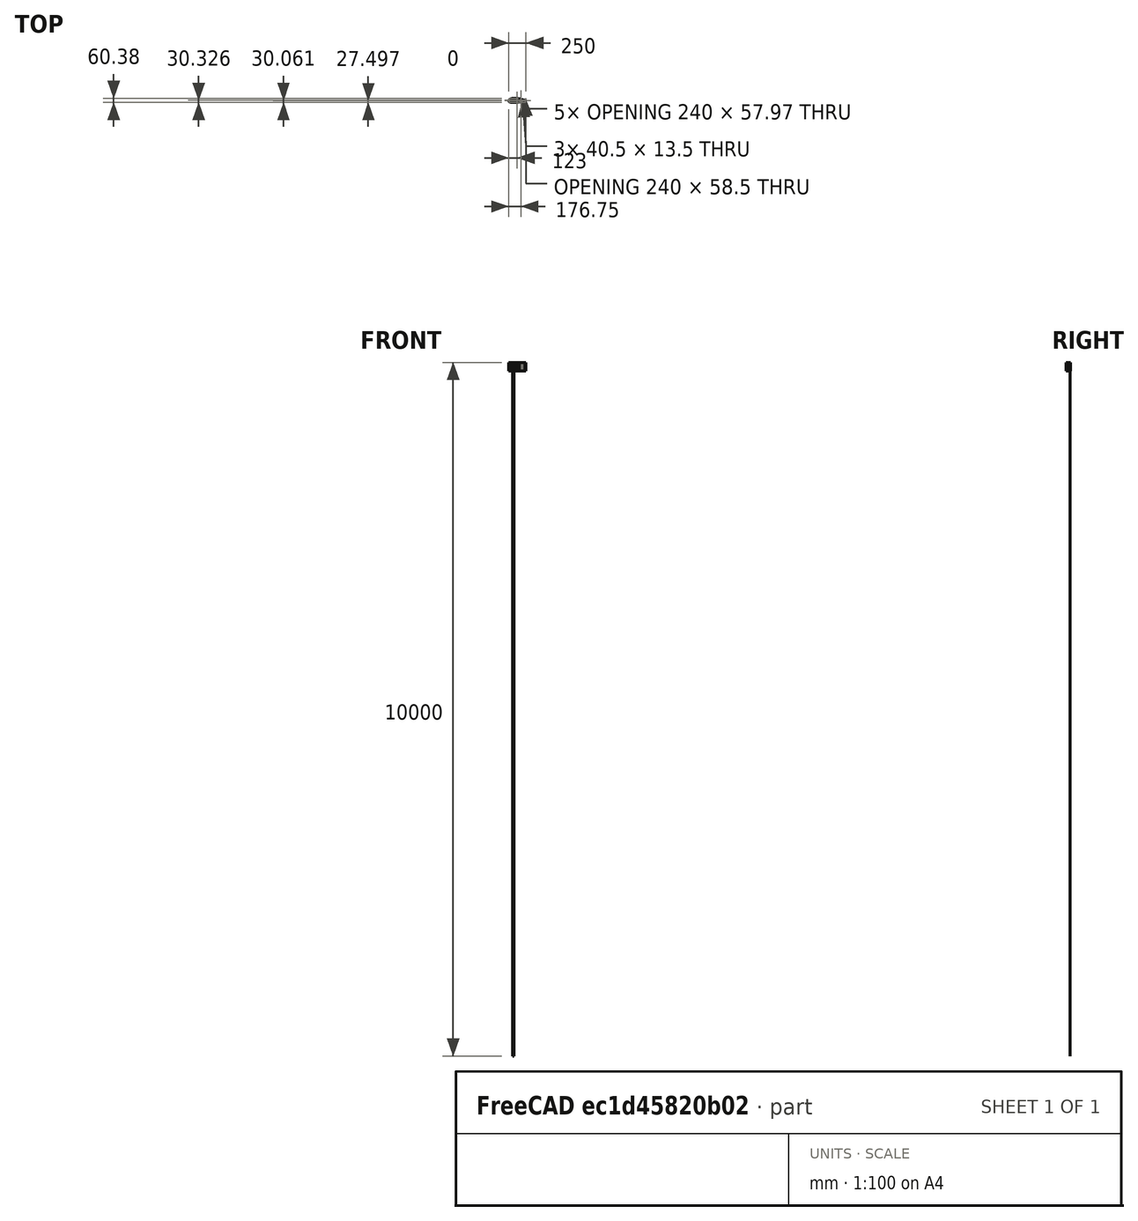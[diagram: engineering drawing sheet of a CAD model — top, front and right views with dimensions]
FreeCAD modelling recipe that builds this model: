
FCSTD DOCUMENT  (FreeCAD 0.16R6712 (Git))
Label: Corp
License: All rights reserved
LicenseURL: http://en.wikipedia.org/wiki/All_rights_reserved
objects: Sketcher::SketchObject×10, PartDesign::Pad×7, Mesh::Feature×7, PartDesign::Pocket×5, App::DocumentObjectGroup×2, Part::Part2DObjectPython×2, Part::Cut×1
note: 37 computed .brp shape members not serialized (recipe doc carries the construction recipe); baked Part::Feature solids carry a one-line shape summary decoded from their .brp

FEATURE [App::DocumentObjectGroup] naca4424
FEATURE [Part::Part2DObjectPython] DWire  # Draft 2D object (typed FeaturePython)
  ChamferSize = 0
  Closed = true
  End = (250,0,0)
  FilletRadius = 0
  Length = 531.973
  MakeFace = true
  Points = (34) [(237.99,5.6,0),(225.8,10.2475,0),(201.16,18.6175,0),(176.218,25.78,0),(151.012,31.685,0),(125.587,36.185,0),(100,39.015,0),(73.5025,39.345,0),+26 more]
  Start = (237.99,5.6,0)
  Subdivisions = 0
FEATURE [PartDesign::Pad] Pad
  Length = 120
  Length2 = 100
  Sketch = -> DWire
  Type = 0
FEATURE [App::DocumentObjectGroup] naca4424001  label="naca4424_interne"
FEATURE [Part::Part2DObjectPython] DWire001  # Draft 2D object (typed FeaturePython)
  ChamferSize = 0
  Closed = true
  End = (243,0.5,0)
  FilletRadius = 0
  Length = 510.694
  MakeFace = true
  Placement = pos=(3,0.5,0) rot=(0,0,1;0rad)
  Points = (34) [(228.47,5.376,0),(216.768,9.8376,0),(193.114,17.8728,0),(169.169,24.7488,0),(144.972,30.4176,0),(120.564,34.7376,0),(96,37.4544,0),+27 more]
  Start = (231.47,5.876,0)
  Subdivisions = 0
FEATURE [PartDesign::Pad] Pad001
  Length = 120
  Length2 = 100
  Placement = pos=(3,0.5,0) rot=(0,0,1;0rad)
  Sketch = -> DWire001
  Type = 0
FEATURE [Part::Cut] Cut  label="Enveloppe"
  Base = -> Pad
  Tool = -> Pad001
FEATURE [Sketcher::SketchObject] Sketch
  ExternalGeometry = -> [Cut]
  Placement = pos=(0,0,120) rot=(0,0,1;0rad)
  Support = -> Cut [Face5]
  sketch-geometry (36):
    g0: LineSegment StartX=25.94 StartY=27.8417 StartZ=0 EndX=25.94 EndY=-15.2288 EndZ=0
    g1: LineSegment StartX=37.1909 StartY=32.1712 StartZ=0 EndX=77 EndY=32.1712 EndZ=0
    g2: LineSegment StartX=25.94 StartY=-15.2288 StartZ=0 EndX=125.433 EndY=-15.2288 EndZ=0
    g3: LineSegment StartX=40.9721 StartY=33.1712 StartZ=0 EndX=77 EndY=33.1712 EndZ=0
    g4: LineSegment StartX=40.9721 StartY=33.1712 StartZ=0 EndX=37.1909 EndY=32.1712 EndZ=0
    g5: LineSegment StartX=135.239 StartY=33.1712 StartZ=0 EndX=140.889 EndY=32.1712 EndZ=0
    g6: LineSegment StartX=25.94 StartY=-16.2288 StartZ=0 EndX=116.78 EndY=-16.2288 EndZ=0
    g7: LineSegment StartX=125.433 StartY=-15.2288 StartZ=0 EndX=116.78 EndY=-16.2288 EndZ=0
    g8: LineSegment StartX=77 StartY=38.2284 StartZ=0 EndX=77 EndY=33.1712 EndZ=0
    g9: LineSegment StartX=77 StartY=30.2284 StartZ=0 EndX=116.5 EndY=30.2284 EndZ=0
    g10: LineSegment StartX=116.5 StartY=30.2284 StartZ=0 EndX=116.5 EndY=10.2284 EndZ=0
    g11: LineSegment StartX=116.5 StartY=10.2284 StartZ=0 EndX=117.5 EndY=10.2284 EndZ=0
    g12: LineSegment StartX=117.5 StartY=10.2284 StartZ=0 EndX=117.5 EndY=32.1712 EndZ=0
    g13: LineSegment StartX=78 StartY=38.2159 StartZ=0 EndX=78 EndY=31.2284 EndZ=0
    g14: LineSegment StartX=78 StartY=31.2284 StartZ=0 EndX=116.5 EndY=31.2284 EndZ=0
    g15: LineSegment StartX=116.5 StartY=31.2284 StartZ=0 EndX=116.5 EndY=36.0189 EndZ=0
    g16: LineSegment StartX=117.5 StartY=33.1712 StartZ=0 EndX=135.239 EndY=33.1712 EndZ=0
    g17: LineSegment StartX=117.5 StartY=32.1712 StartZ=0 EndX=140.889 EndY=32.1712 EndZ=0
    g18: LineSegment StartX=77 StartY=32.1712 StartZ=0 EndX=77 EndY=30.2284 EndZ=0
    g19: LineSegment StartX=117.5 StartY=33.1712 StartZ=0 EndX=117.5 EndY=35.9083 EndZ=0
    g20: LineSegment StartX=77 StartY=38.2284 StartZ=0 EndX=78 EndY=38.2159 EndZ=0
    g21: LineSegment StartX=116.5 StartY=36.0189 StartZ=0 EndX=117.5 EndY=35.9083 EndZ=0
    g22: Circle CenterX=5.5894 CenterY=1.00227 CenterZ=0 NormalX=0 NormalY=0 NormalZ=1 Radius=2.5
    g23: ArcOfCircle CenterX=5.5894 CenterY=1.00227 CenterZ=0 NormalX=0 NormalY=0 NormalZ=1 Radius=3.5 StartAngle=4.43289 EndAngle=8.51667
    g24: LineSegment StartX=3.43607 StartY=3.76147 StartZ=0 EndX=3 EndY=0.5 EndZ=0
    g25: LineSegment StartX=3 StartY=0.5 StartZ=0 EndX=4.62383 EndY=-2.3619 EndZ=0
    g26: Circle CenterX=234.867 CenterY=1.53378 CenterZ=0 NormalX=0 NormalY=0 NormalZ=1 Radius=2.5
    g27: ArcOfCircle CenterX=234.867 CenterY=1.53378 CenterZ=0 NormalX=0 NormalY=0 NormalZ=1 Radius=3.5 StartAngle=1.90968 EndAngle=4.12064
    g28: ArcOfCircle CenterX=234.867 CenterY=1.53378 CenterZ=0 NormalX=0 NormalY=0 NormalZ=1 Radius=3.5 StartAngle=5.67102 EndAngle=6.64248
    g29: LineSegment StartX=233.704 StartY=4.83472 StartZ=0 EndX=238.144 EndY=2.76443 EndZ=0
    g30: LineSegment StartX=232.915 StartY=-1.37109 StartZ=0 EndX=237.732 EndY=-0.477447 EndZ=0
    g31: LineSegment StartX=24.94 StartY=-16.296 StartZ=0 EndX=25.94 EndY=-16.5246 EndZ=0
    g32: LineSegment StartX=25.94 StartY=-16.5246 StartZ=0 EndX=25.94 EndY=-16.2288 EndZ=0
    g33: LineSegment StartX=24.94 StartY=27.4402 StartZ=0 EndX=25.94 EndY=27.8417 EndZ=0
    g34: LineSegment [constr] StartX=25.94 StartY=-15.2288 StartZ=0 EndX=25.94 EndY=-16.2288 EndZ=0
    g35: LineSegment StartX=24.94 StartY=27.4402 StartZ=0 EndX=24.94 EndY=-16.296 EndZ=0
  constraints (101):
    c: Vertical(g0)
    c: Horizontal(g1)
    c: Horizontal(g2)
    c: PointOnObject(g1,g-3)
    c: DistanceY(g1,g-4) = 6.1
    c: PointOnObject(g17,g-5)
    c: PointOnObject(g16,g-5)
    c: Horizontal(g3)
    c: PointOnObject(g3,g-3)
    c: Coincident(g4,g3)
    c: Coincident(g4,g1)
    c: Coincident(g5,g16)
    c: Coincident(g5,g17)
    c: DistanceY(g17,g16) = 1
    c: Horizontal(g6)
    c: PointOnObject(g2,g-8)
    c: PointOnObject(g6,g-8)
    c: Coincident(g7,g2)
    c: Coincident(g7,g6)
    c: Coincident(g0,g2)
    c: DistanceY(g6,g0) = 1
    c: Vertical(g8)
    c: Coincident(g9,g18)
    c: Horizontal(g9)
    c: Coincident(g10,g9)
    c: Vertical(g10)
    c: Coincident(g11,g10)
    c: Horizontal(g11)
    c: Vertical(g12)
    c: PointOnObject(g8,g-4)
    c: DistanceY(g18,g8) = 8
    c: DistanceX(g8,g-4) = 22
    c: DistanceX(g9,g9) = 39.5
    c: DistanceX(g11,g11) = 1
    c: Coincident(g11,g12)
    c: PointOnObject(g19,g-9)
    c: PointOnObject(g13,g-4)
    c: Vertical(g13)
    c: Coincident(g14,g13)
    c: Horizontal(g14)
    c: Coincident(g15,g14)
    c: PointOnObject(g15,g-9)
    c: Vertical(g15)
    c: Tangent(g3,g16)
    c: Tangent(g1,g17)
    c: Coincident(g8,g3)
    c: Coincident(g18,g1)
    c: Tangent(g8,g18)
    c: Coincident(g12,g17)
    c: Coincident(g19,g16)
    c: Tangent(g12,g19)
    c: DistanceX(g15,g19) = 1
    c: DistanceY(g9,g14) = 1
    c: DistanceX(g8,g13) = 1
    c: Coincident(g20,g8)
    c: Coincident(g20,g13)
    c: Coincident(g21,g15)
    c: Coincident(g21,g19)
    c: DistanceY(g10,g10) = 20
    c: Tangent(g22,g-10)
    c: Radius(g22) = 2.5
    c: Coincident(g23,g22)
    c: PointOnObject(g23,g-10)
    c: Coincident(g24,g-10)
    c: Tangent(g24,g22)
    c: Coincident(g25,g24)
    c: Coincident(g25,g23)
    c: Tangent(g26,g-11)
    c: Tangent(g26,g-12)
    c: Radius(g26) = 2.5
    c: Radius(g23) = 3.5
    c: Coincident(g27,g26)
    c: PointOnObject(g27,g-11)
    c: PointOnObject(g27,g-12)
    c: Radius(g27) = 3.5
    c: Coincident(g28,g26)
    c: PointOnObject(g28,g-11)
    c: PointOnObject(g28,g-12)
    c: Radius(g28) = 3.5
    c: Coincident(g29,g27)
    c: Coincident(g29,g28)
    c: Coincident(g30,g28)
    c: Coincident(g32,g6)
    c: Vertical(g32)
    c: Coincident(g33,g0)
    c: DistanceX(g33,g0) = 1
    c: Coincident(g30,g27)
    c: Coincident(g23,g24)
    c: PointOnObject(g23,g-13)
    c: DistanceX(g-7,g31) = 8
    c: PointOnObject(g0,g-6)
    c: PointOnObject(g33,g-6)
    c: PointOnObject(g31,g-16)
    c: Vertical(g34)
    c: Coincident(g34,g6)
    c: Coincident(g0,g34)
    c: DistanceX(g31,g31) = 1
    c: PointOnObject(g32,g-16)
    c: Coincident(g32,g31)
    c: Coincident(g35,g33)
    c: Coincident(g35,g31)
FEATURE [PartDesign::Pad] Pad002  label="Interne__Support_Composant"
  Length = 120
  Length2 = 100
  Reversed = true
  Sketch = -> Sketch
  Type = 0
FEATURE [Mesh::Feature] Support_Composant
  Placement = pos=(116,-15,119) rot=(0,1,0;3.14159rad)
FEATURE [Mesh::Feature] Gouverne_Profondeur
  Placement = pos=(252,1,-2.5) rot=(0,0,1;0rad)
FEATURE [Sketcher::SketchObject] Sketch001
  ExternalGeometry = -> [Pad002]
  Placement = pos=(0,0,0) rot=(1,0,0;3.14159rad)
  Support = -> Pad002 [Face4]
  sketch-geometry (20):
    g0: LineSegment StartX=156.5 StartY=11.529 StartZ=0 EndX=156.5 EndY=1.29344 EndZ=0
    g1: LineSegment StartX=156.5 StartY=11.529 StartZ=0 EndX=155.5 EndY=11.655 EndZ=0
    g2: LineSegment StartX=155.5 StartY=11.655 StartZ=0 EndX=155.5 EndY=-29.1539 EndZ=0
    g3: LineSegment StartX=155.5 StartY=-29.1539 StartZ=0 EndX=156.5 EndY=-28.9197 EndZ=0
    g4: LineSegment StartX=156.5 StartY=0.293445 StartZ=0 EndX=197 EndY=0.293445 EndZ=0
    g5: LineSegment StartX=156.5 StartY=1.29344 StartZ=0 EndX=197 EndY=1.29344 EndZ=0
    g6: LineSegment StartX=197 StartY=1.29344 StartZ=0 EndX=197 EndY=6.29344 EndZ=0
    g7: LineSegment StartX=197 StartY=6.29344 StartZ=0 EndX=198 EndY=6.16056 EndZ=0
    g8: LineSegment StartX=198 StartY=6.16056 StartZ=0 EndX=198 EndY=-17.732 EndZ=0
    g9: LineSegment StartX=197 StartY=0.293445 StartZ=0 EndX=197 EndY=-13.2066 EndZ=0
    g10: LineSegment StartX=197 StartY=-18.0717 StartZ=0 EndX=198 EndY=-17.732 EndZ=0
    g11: LineSegment StartX=156.5 StartY=0.293445 StartZ=0 EndX=156.5 EndY=-13.2066 EndZ=0
    g12: LineSegment [constr] StartX=197 StartY=1.29344 StartZ=0 EndX=197 EndY=0.293445 EndZ=0
    g13: LineSegment [constr] StartX=156.5 StartY=1.29344 StartZ=0 EndX=156.5 EndY=0.293445 EndZ=0
    g14: LineSegment StartX=156.5 StartY=-13.2066 StartZ=0 EndX=197 EndY=-13.2066 EndZ=0
    g15: LineSegment StartX=156.5 StartY=-14.2066 StartZ=0 EndX=197 EndY=-14.2066 EndZ=0
    g16: LineSegment StartX=197 StartY=-14.2066 StartZ=0 EndX=197 EndY=-18.0717 EndZ=0
    g17: LineSegment StartX=156.5 StartY=-14.2066 StartZ=0 EndX=156.5 EndY=-28.9197 EndZ=0
    g18: LineSegment [constr] StartX=156.5 StartY=-13.2066 StartZ=0 EndX=156.5 EndY=-14.2066 EndZ=0
    g19: LineSegment [constr] StartX=197 StartY=-13.2066 StartZ=0 EndX=197 EndY=-14.2066 EndZ=0
  constraints (56):
    c: Vertical(g0)
    c: Coincident(g1,g0)
    c: PointOnObject(g2,g1)
    c: Vertical(g2)
    c: Coincident(g3,g2)
    c: Horizontal(g4)
    c: Horizontal(g5)
    c: Coincident(g6,g5)
    c: Coincident(g8,g7)
    c: Vertical(g8)
    c: Coincident(g9,g4)
    c: Vertical(g9)
    c: Coincident(g10,g16)
    c: Coincident(g10,g8)
    c: Coincident(g1,g2)
    c: PointOnObject(g1,g-6)
    c: PointOnObject(g0,g-6)
    c: Coincident(g0,g5)
    c: Coincident(g11,g4)
    c: Tangent(g0,g11)
    c: DistanceX(g5,g5) = 40.5
    c: Vertical(g6)
    c: Coincident(g6,g7)
    c: PointOnObject(g6,g-3)
    c: PointOnObject(g7,g-3)
    c: Coincident(g12,g5)
    c: Coincident(g12,g4)
    c: Vertical(g12)
    c: Coincident(g13,g0)
    c: Coincident(g13,g4)
    c: PointOnObject(g16,g-4)
    c: PointOnObject(g8,g-4)
    c: DistanceX(g5,g7) = 1
    c: DistanceY(g4,g0) = 1
    c: DistanceX(g1,g0) = 1
    c: DistanceY(g6,g6) = 5
    c: Horizontal(g14)
    c: Horizontal(g15)
    c: Coincident(g9,g14)
    c: Coincident(g16,g15)
    c: Tangent(g9,g16)
    c: Coincident(g11,g14)
    c: Coincident(g17,g15)
    c: Tangent(g11,g17)
    c: Coincident(g18,g11)
    c: PointOnObject(g18,g17)
    c: Coincident(g18,g15)
    c: Coincident(g19,g15)
    c: Vertical(g19)
    c: DistanceY(g19,g19) = 1
    c: Coincident(g9,g19)
    c: DistanceY(g9,g9) = 13.5
    c: Coincident(g17,g3)
    c: PointOnObject(g2,g-5)
    c: PointOnObject(g3,g-5)
    c: DistanceX(g7,g-7) = 45
FEATURE [PartDesign::Pad] Pad003  label="Interne___Support_servos_arrieres"
  Length = 120
  Length2 = 100
  Reversed = true
  Sketch = -> Sketch001
  Type = 0
FEATURE [Sketcher::SketchObject] Sketch002
  ExternalGeometry = -> [Pad003]
  Placement = pos=(0,0,120) rot=(0,0,1;0rad)
  Support = -> Pad003 [Face92]
  sketch-geometry (4):
    g0: LineSegment StartX=139.889 StartY=32.1712 StartZ=0 EndX=139.889 EndY=-13.5582 EndZ=0
    g1: LineSegment StartX=140.889 StartY=32.1712 StartZ=0 EndX=140.889 EndY=-13.4427 EndZ=0
    g2: LineSegment StartX=139.889 StartY=32.1712 StartZ=0 EndX=140.889 EndY=32.1712 EndZ=0
    g3: LineSegment StartX=139.889 StartY=-13.5582 StartZ=0 EndX=140.889 EndY=-13.4427 EndZ=0
  constraints (11):
    c: Vertical(g0)
    c: Vertical(g1)
    c: Coincident(g2,g0)
    c: Coincident(g2,g1)
    c: Coincident(g3,g0)
    c: Coincident(g3,g1)
    c: PointOnObject(g1,g-3)
    c: PointOnObject(g0,g-3)
    c: DistanceX(g0,g1) = 1
    c: Coincident(g1,g-4)
    c: PointOnObject(g0,g-4)
FEATURE [PartDesign::Pad] Pad004  label="Interne___Renfort"
  Length = 120
  Length2 = 100
  Reversed = true
  Sketch = -> Sketch002
  Type = 0
FEATURE [Sketcher::SketchObject] Sketch003
  ExternalGeometry = -> [Pad004]
  Placement = pos=(20.2632,70.5639,0) rot=(0.099027,0.703631,0.703631;2.94418rad)
  Support = -> Pad004 [Face7]
  sketch-geometry (5):
    g0: LineSegment StartX=-228.208 StartY=63 StartZ=0 EndX=-183.208 EndY=63 EndZ=0
    g1: LineSegment StartX=-183.208 StartY=63 StartZ=0 EndX=-183.208 EndY=57 EndZ=0
    g2: LineSegment StartX=-183.208 StartY=57 StartZ=0 EndX=-228.208 EndY=57 EndZ=0
    g3: LineSegment StartX=-228.208 StartY=57 StartZ=0 EndX=-228.208 EndY=63 EndZ=0
    g4: LineSegment [constr] StartX=-228.208 StartY=60 StartZ=0 EndX=-183.208 EndY=60 EndZ=0
  constraints (16):
    c: Coincident(g0,g1)
    c: Coincident(g1,g2)
    c: Coincident(g2,g3)
    c: Coincident(g3,g0)
    c: Horizontal(g0)
    c: Horizontal(g2)
    c: Vertical(g1)
    c: Vertical(g3)
    c: Horizontal(g4)
    c: PointOnObject(g4,g1)
    c: PointOnObject(g4,g3)
    c: DistanceY(g1,g1) = 6
    c: Symmetric(g1,g0,g4)
    c: Symmetric(g-3,g-4,g4)
    c: DistanceX(g0,g0) = 45
    c: DistanceX(g-3,g0) = 5
FEATURE [PartDesign::Pocket] Pocket  label="Socle___Gouverne_direction"
  Length = 5
  Sketch = -> Sketch003
  Type = 0
FEATURE [Mesh::Feature] Gouverne_Direction
  Placement = pos=(237,1,63) rot=(-0.97312,0.162845,-0.162845;1.59804rad)
FEATURE [Sketcher::SketchObject] Sketch004
  ExternalGeometry = -> [Pocket]
  Placement = pos=(0,0,120) rot=(0,0,1;0rad)
  Support = -> Pocket [Face149]
  sketch-geometry (4):
    g0: LineSegment StartX=156.5 StartY=9.20656 StartZ=0 EndX=139.889 EndY=9.20656 EndZ=0
    g1: LineSegment StartX=139.889 StartY=9.20656 StartZ=0 EndX=139.889 EndY=4.20656 EndZ=0
    g2: LineSegment StartX=139.889 StartY=4.20656 StartZ=0 EndX=156.5 EndY=4.20656 EndZ=0
    g3: LineSegment StartX=156.5 StartY=4.20656 StartZ=0 EndX=156.5 EndY=9.20656 EndZ=0
  constraints (12):
    c: Coincident(g0,g1)
    c: Coincident(g1,g2)
    c: Coincident(g2,g3)
    c: Coincident(g3,g0)
    c: Horizontal(g0)
    c: Horizontal(g2)
    c: Vertical(g1)
    c: Vertical(g3)
    c: DistanceY(g1,g1) = 5
    c: PointOnObject(g0,g-3)
    c: PointOnObject(g0,g-5)
    c: DistanceY(g0,g-3) = 4
FEATURE [PartDesign::Pocket] Pocket001  label="Goutiere___cables_servos_arrieres"
  Length = 40
  Sketch = -> Sketch004
  Type = 0
FEATURE [Sketcher::SketchObject] Sketch005
  ExternalGeometry = -> [Pocket001]
  Placement = pos=(0,0,120) rot=(0,0,1;0rad)
  Support = -> Pocket001 [Face151]
  sketch-geometry (4):
    g0: LineSegment StartX=55 StartY=33.1712 StartZ=0 EndX=77 EndY=33.1712 EndZ=0
    g1: LineSegment StartX=77 StartY=33.1712 StartZ=0 EndX=77 EndY=32.1712 EndZ=0
    g2: LineSegment StartX=77 StartY=32.1712 StartZ=0 EndX=55 EndY=32.1712 EndZ=0
    g3: LineSegment StartX=55 StartY=32.1712 StartZ=0 EndX=55 EndY=33.1712 EndZ=0
  constraints (11):
    c: Coincident(g0,g1)
    c: Coincident(g1,g2)
    c: Coincident(g2,g3)
    c: Coincident(g3,g0)
    c: Horizontal(g0)
    c: Horizontal(g2)
    c: Vertical(g1)
    c: Vertical(g3)
    c: DistanceX(g2,g2) = 22
    c: Coincident(g0,g-3)
    c: Coincident(g1,g-4)
FEATURE [PartDesign::Pocket] Pocket002  label="Goutiere___Cables_carte_SPRACING"
  Length = 5
  Sketch = -> Sketch005
  Type = 1
FEATURE [Sketcher::SketchObject] Sketch006
  ExternalGeometry = -> [Pocket002]
  Placement = pos=(0,0,120) rot=(0,0,1;0rad)
  Support = -> Pocket002 [Face155]
  sketch-geometry (4):
    g0: LineSegment StartX=54 StartY=36.0503 StartZ=0 EndX=55 EndY=36.2161 EndZ=0
    g1: LineSegment StartX=55 StartY=36.2161 StartZ=0 EndX=55 EndY=33.1712 EndZ=0
    g2: LineSegment StartX=55 StartY=33.1712 StartZ=0 EndX=54 EndY=33.1712 EndZ=0
    g3: LineSegment StartX=54 StartY=33.1712 StartZ=0 EndX=54 EndY=36.0503 EndZ=0
  constraints (11):
    c: Coincident(g0,g1)
    c: Coincident(g1,g2)
    c: Coincident(g2,g3)
    c: Coincident(g3,g0)
    c: Horizontal(g2)
    c: Vertical(g1)
    c: Vertical(g3)
    c: PointOnObject(g0,g-3)
    c: PointOnObject(g0,g-3)
    c: DistanceX(g2,g2) = 1
    c: Coincident(g1,g-4)
FEATURE [PartDesign::Pad] Pad005  label="Interne___Renfort_2"
  Length = 120
  Length2 = 100
  Reversed = true
  Sketch = -> Sketch006
  Type = 0
FEATURE [Sketcher::SketchObject] Sketch007
  ExternalGeometry = -> [Pad005]
  Placement = pos=(0,0,120) rot=(0,0,1;0rad)
  Support = -> Pad005 [Face108]
  sketch-geometry (8):
    g0: LineSegment StartX=66.94 StartY=-16.2288 StartZ=0 EndX=66.94 EndY=-19.2288 EndZ=0
    g1: LineSegment StartX=66.94 StartY=-19.2288 StartZ=0 EndX=51.94 EndY=-19.2288 EndZ=0
    g2: LineSegment StartX=51.94 StartY=-19.2288 StartZ=0 EndX=51.94 EndY=-16.2288 EndZ=0
    g3: LineSegment StartX=66.94 StartY=-16.2288 StartZ=0 EndX=67.94 EndY=-16.2288 EndZ=0
    g4: LineSegment StartX=67.94 StartY=-16.2288 StartZ=0 EndX=67.94 EndY=-20.2288 EndZ=0
    g5: LineSegment StartX=67.94 StartY=-20.2288 StartZ=0 EndX=50.94 EndY=-20.2288 EndZ=0
    g6: LineSegment StartX=50.94 StartY=-20.2288 StartZ=0 EndX=50.94 EndY=-16.2288 EndZ=0
    g7: LineSegment StartX=50.94 StartY=-16.2288 StartZ=0 EndX=51.94 EndY=-16.2288 EndZ=0
  constraints (24):
    c: Coincident(g0,g1)
    c: Coincident(g1,g2)
    c: Horizontal(g1)
    c: Vertical(g0)
    c: Vertical(g2)
    c: DistanceY(g0,g0) = 3
    c: DistanceX(g2,g0) = 15
    c: PointOnObject(g0,g-3)
    c: Horizontal(g3)
    c: Vertical(g4)
    c: Coincident(g5,g4)
    c: Horizontal(g5)
    c: Coincident(g6,g5)
    c: PointOnObject(g6,g-3)
    c: Vertical(g6)
    c: Coincident(g7,g6)
    c: Coincident(g7,g2)
    c: DistanceX(g6,g2) = 1
    c: DistanceX(g0,g3) = 1
    c: Coincident(g4,g3)
    c: DistanceY(g5,g1) = 1
    c: DistanceX(g-3,g2) = 26
    c: Coincident(g0,g3)
    c: PointOnObject(g2,g-3)
FEATURE [Mesh::Feature] Aile_double_babord_2
  Placement = pos=(45.9,-18.25,120) rot=(0,0,1;0rad)
FEATURE [Mesh::Feature] Aile_double_tribord_2
  Placement = pos=(45.9,-18.3,-1) rot=(0,0,1;0rad)
FEATURE [Mesh::Feature] Aile_double_milieu
  Placement = pos=(45.9,81.7,-0.5) rot=(0,0,1;0rad)
FEATURE [PartDesign::Pad] Pad006  label="Interne__Support_ailes"
  Length = 120
  Length2 = 100
  Reversed = true
  Sketch = -> Sketch007
  Type = 0
FEATURE [Sketcher::SketchObject] Sketch008
  ExternalGeometry = -> [Pad006]
  Placement = pos=(0,0,120) rot=(0,0,1;0rad)
  Support = -> Pad006 [Face164]
  sketch-geometry (16):
    g0: LineSegment StartX=24.94 StartY=5 StartZ=0 EndX=25.94 EndY=5 EndZ=0
    g1: LineSegment StartX=25.94 StartY=5 StartZ=0 EndX=25.94 EndY=-5 EndZ=0
    g2: LineSegment StartX=25.94 StartY=-5 StartZ=0 EndX=24.94 EndY=-5 EndZ=0
    g3: LineSegment StartX=24.94 StartY=-5 StartZ=0 EndX=24.94 EndY=5 EndZ=0
    g4: LineSegment StartX=139.889 StartY=4.20656 StartZ=0 EndX=140.889 EndY=4.20656 EndZ=0
    g5: LineSegment StartX=140.889 StartY=4.20656 StartZ=0 EndX=140.889 EndY=-4.20656 EndZ=0
    g6: LineSegment StartX=140.889 StartY=-4.20656 StartZ=0 EndX=139.889 EndY=-4.20656 EndZ=0
    g7: LineSegment StartX=139.889 StartY=-4.20656 StartZ=0 EndX=139.889 EndY=4.20656 EndZ=0
    g8: LineSegment StartX=155.5 StartY=26.2066 StartZ=0 EndX=156.5 EndY=26.2066 EndZ=0
    g9: LineSegment StartX=156.5 StartY=26.2066 StartZ=0 EndX=156.5 EndY=16.2066 EndZ=0
    g10: LineSegment StartX=156.5 StartY=16.2066 StartZ=0 EndX=155.5 EndY=16.2066 EndZ=0
    g11: LineSegment StartX=155.5 StartY=16.2066 StartZ=0 EndX=155.5 EndY=26.2066 EndZ=0
    g12: LineSegment StartX=197 StartY=16.7066 StartZ=0 EndX=198 EndY=16.7066 EndZ=0
    g13: LineSegment StartX=198 StartY=16.7066 StartZ=0 EndX=198 EndY=14.2066 EndZ=0
    g14: LineSegment StartX=198 StartY=14.2066 StartZ=0 EndX=197 EndY=14.2066 EndZ=0
    g15: LineSegment StartX=197 StartY=14.2066 StartZ=0 EndX=197 EndY=16.7066 EndZ=0
  constraints (46):
    c: Coincident(g0,g1)
    c: Coincident(g1,g2)
    c: Coincident(g2,g3)
    c: Coincident(g3,g0)
    c: Horizontal(g0)
    c: Horizontal(g2)
    c: Vertical(g1)
    c: Vertical(g3)
    c: PointOnObject(g2,g-4)
    c: PointOnObject(g0,g-3)
    c: DistanceY(g1,g0) = 10
    c: Symmetric(g0,g2,g-1)
    c: Coincident(g4,g5)
    c: Coincident(g5,g6)
    c: Coincident(g6,g7)
    c: Coincident(g7,g4)
    c: Horizontal(g4)
    c: Horizontal(g6)
    c: Vertical(g5)
    c: Vertical(g7)
    c: Coincident(g4,g-5)
    c: Coincident(g4,g-6)
    c: Symmetric(g6,g4,g-1)
    c: Coincident(g8,g9)
    c: Coincident(g9,g10)
    c: Coincident(g10,g11)
    c: Coincident(g11,g8)
    c: Horizontal(g8)
    c: Horizontal(g10)
    c: Vertical(g9)
    c: Vertical(g11)
    c: PointOnObject(g8,g-8)
    c: PointOnObject(g10,g-7)
    c: DistanceY(g9,g8) = 10
    c: DistanceY(g-8,g9) = 2
    c: Coincident(g12,g13)
    c: Coincident(g13,g14)
    c: Coincident(g14,g15)
    c: Coincident(g15,g12)
    c: Horizontal(g12)
    c: Horizontal(g14)
    c: Vertical(g13)
    c: Vertical(g15)
    c: Coincident(g14,g-9)
    c: PointOnObject(g12,g-10)
    c: DistanceY(g13,g12) = 2.5
FEATURE [PartDesign::Pocket] Pocket003  label="Goutiere__cables_moteurs_1"
  Length = 20
  Sketch = -> Sketch008
  Type = 0
FEATURE [Sketcher::SketchObject] Sketch009
  ExternalGeometry = -> [Pocket003]
  Placement = pos=(0,0,0) rot=(1,0,0;3.14159rad)
  Support = -> Pocket003 [Face54]
  sketch-geometry (16):
    g0: LineSegment StartX=24.94 StartY=5 StartZ=0 EndX=25.94 EndY=5 EndZ=0
    g1: LineSegment StartX=25.94 StartY=5 StartZ=0 EndX=25.94 EndY=-5 EndZ=0
    g2: LineSegment StartX=25.94 StartY=-5 StartZ=0 EndX=24.94 EndY=-5 EndZ=0
    g3: LineSegment StartX=24.94 StartY=-5 StartZ=0 EndX=24.94 EndY=5 EndZ=0
    g4: LineSegment StartX=139.889 StartY=5 StartZ=0 EndX=140.889 EndY=5 EndZ=0
    g5: LineSegment StartX=140.889 StartY=5 StartZ=0 EndX=140.889 EndY=-5 EndZ=0
    g6: LineSegment StartX=140.889 StartY=-5 StartZ=0 EndX=139.889 EndY=-5 EndZ=0
    g7: LineSegment StartX=139.889 StartY=-5 StartZ=0 EndX=139.889 EndY=5 EndZ=0
    g8: LineSegment StartX=155.5 StartY=-16.2066 StartZ=0 EndX=156.5 EndY=-16.2066 EndZ=0
    g9: LineSegment StartX=156.5 StartY=-16.2066 StartZ=0 EndX=156.5 EndY=-26.2066 EndZ=0
    g10: LineSegment StartX=156.5 StartY=-26.2066 StartZ=0 EndX=155.5 EndY=-26.2066 EndZ=0
    g11: LineSegment StartX=155.5 StartY=-26.2066 StartZ=0 EndX=155.5 EndY=-16.2066 EndZ=0
    g12: LineSegment StartX=197 StartY=-14.2066 StartZ=0 EndX=198 EndY=-14.2066 EndZ=0
    g13: LineSegment StartX=198 StartY=-14.2066 StartZ=0 EndX=198 EndY=-16.7066 EndZ=0
    g14: LineSegment StartX=198 StartY=-16.7066 StartZ=0 EndX=197 EndY=-16.7066 EndZ=0
    g15: LineSegment StartX=197 StartY=-16.7066 StartZ=0 EndX=197 EndY=-14.2066 EndZ=0
  constraints (47):
    c: Coincident(g0,g1)
    c: Coincident(g1,g2)
    c: Coincident(g2,g3)
    c: Coincident(g3,g0)
    c: Horizontal(g0)
    c: Horizontal(g2)
    c: Vertical(g1)
    c: Vertical(g3)
    c: Coincident(g4,g5)
    c: Coincident(g5,g6)
    c: Coincident(g6,g7)
    c: Coincident(g7,g4)
    c: Horizontal(g4)
    c: Horizontal(g6)
    c: Vertical(g5)
    c: Vertical(g7)
    c: Coincident(g8,g9)
    c: Coincident(g9,g10)
    c: Coincident(g10,g11)
    c: Coincident(g11,g8)
    c: Horizontal(g8)
    c: Horizontal(g10)
    c: Vertical(g9)
    c: Vertical(g11)
    c: Coincident(g12,g13)
    c: Coincident(g13,g14)
    c: Coincident(g14,g15)
    c: Coincident(g15,g12)
    c: Horizontal(g12)
    c: Horizontal(g14)
    c: Vertical(g13)
    c: Vertical(g15)
    c: PointOnObject(g12,g-10)
    c: Coincident(g12,g-9)
    c: DistanceY(g14,g12) = 2.5
    c: DistanceY(g5,g5) = 10
    c: PointOnObject(g4,g-6)
    c: PointOnObject(g4,g-5)
    c: Symmetric(g5,g4,g-1)
    c: PointOnObject(g8,g-7)
    c: PointOnObject(g8,g-8)
    c: DistanceY(g10,g8) = 10
    c: DistanceY(g8,g-8) = 2
    c: PointOnObject(g0,g-4)
    c: PointOnObject(g0,g-3)
    c: Symmetric(g0,g1,g-1)
    c: DistanceY(g1,g0) = 10
FEATURE [PartDesign::Pocket] Pocket004  label="Goutiere__cables_moteurs_2"
  Length = 20
  Sketch = -> Sketch009
  Type = 0
FEATURE [Mesh::Feature] Guignol_Moteur_Avant
  Placement = pos=(9,-2,127.5) rot=(0,1,0;3.14159rad)
